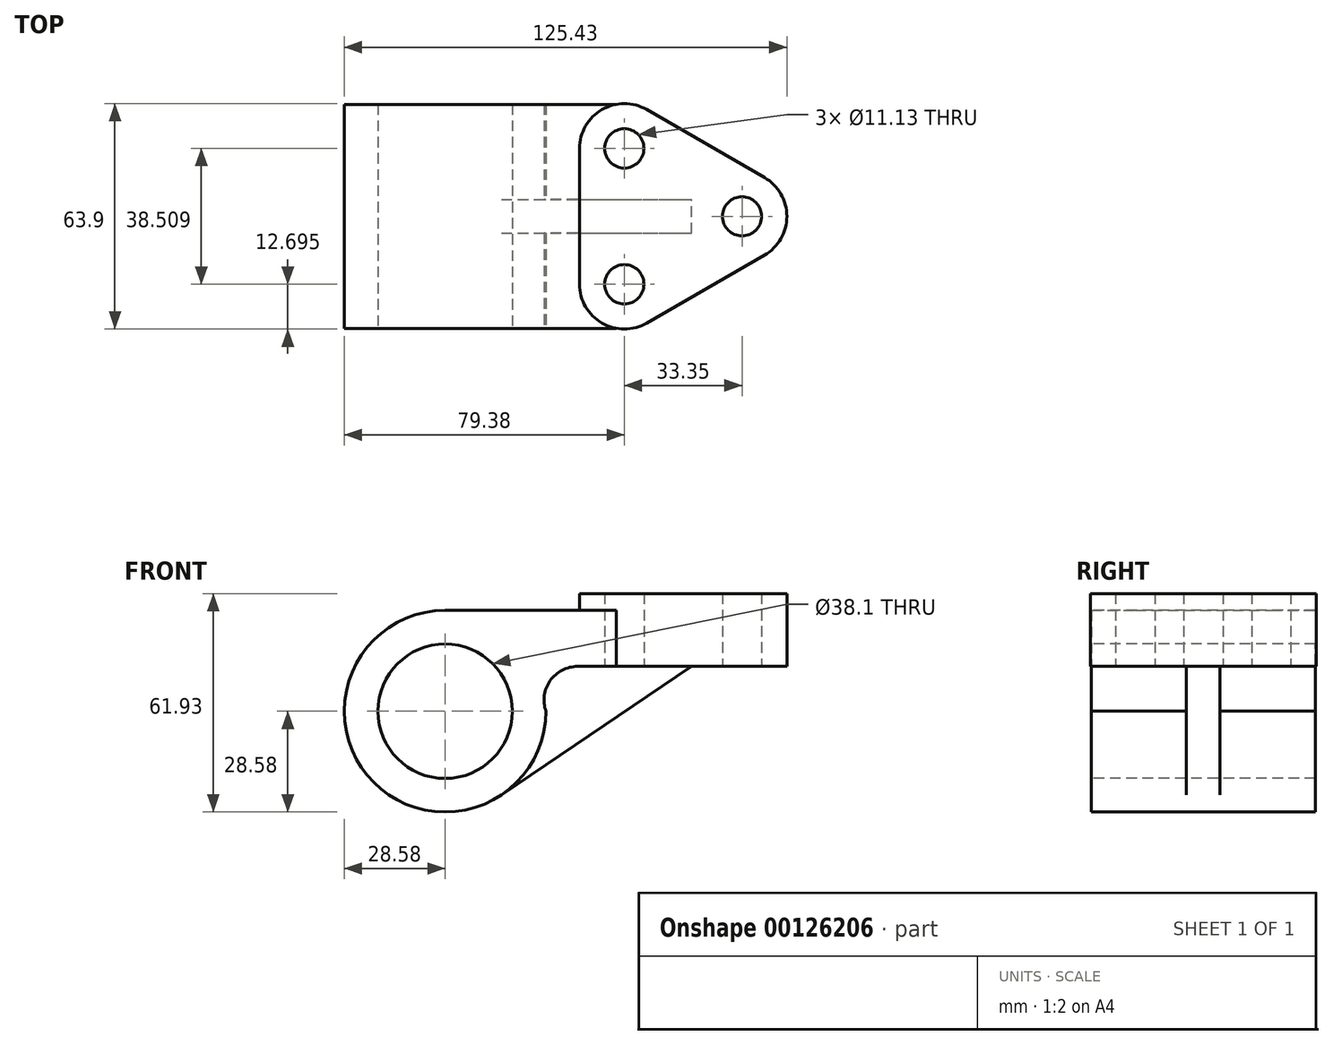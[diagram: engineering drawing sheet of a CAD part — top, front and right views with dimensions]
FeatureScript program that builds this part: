
annotation { "Feature Type Name" : "Feature", "Feature Type Description" : "" }
export const myFeature = defineFeature(function(context is Context, id is Id, definition is map)
    precondition{}
    {
        {
            var Q0;
            Q0=qCreatedBy(makeId("Front.planeOp"),FACE);
            var sketch = newSketch(context, id + "F0", { "sketchPlane" : qUnion([Q0])});
            skCircle(sketch, "E0", {"center": v(0, 0) * mm, "radius": 19.05 * mm});
            skArc(sketch, "E1", {"start": v(37.56, 12.7) * mm, "mid": v(29.78, 8.67) * mm, "end": v(28.58, 0) * mm});
            skLineSegment(sketch, "E2", {"start": v(37.56, 12.7) * mm, "end": v(50.8, 12.7) * mm});
            skLineSegment(sketch, "E3", {"start": v(0, 28.58) * mm, "end": v(50.8, 28.58) * mm});
            skArc(sketch, "E4", {"start": v(0, 28.58) * mm, "mid": v(-20.2, -20.2) * mm, "end": v(28.58, 0) * mm});
            skLineSegment(sketch, "E5", {"start": v(50.8, 28.58) * mm, "end": v(50.8, 12.7) * mm});
            skSolve(sketch);
        }
        {
            var Q0;
            Q0 = qSketchRegion(id + "F0", true);
            extrude(context, id + "F1", {"entities" : qUnion([Q0]), "endBound" : BoundingType.SYMMETRIC, "oppositeDirection" : true, "depth" : 63.5 * mm});
        }
        {
            var Q0;
            Q0=makeQuery(id+"F1.opExtrude","SWEPT_FACE",FACE,{"disambiguationData":[OSD([sQuery(id+"F0.wireOp",EDGE,"E3")])]});
            var sketch = newSketch(context, id + "F2", { "sketchPlane" : qUnion([Q0])});
            skSolve(sketch);
        }
        {
            var Q0;
            {var subQ0=sQuery(id+"F0.wireOp",EDGE,"E3");Q0=makeQuery(id+"F2.imprint","IMPRINT",FACE,{"disambiguationData":[TD([[makeQuery(id+"F2.imprint","IMPRINT",EDGE,{"derivedFrom":makeQuery(id+"F1.opExtrude","CAP_EDGE",EDGE,{"disambiguationData":[OSD([subQ0])],"isStart":true})}),1.0]])]});}
            var sketch = newSketch(context, id + "F3", { "sketchPlane" : qUnion([Q0])});
            skLineSegment(sketch, "E6", {"start": v(0, 0) * mm, "end": v(130.51, 0) * mm, "construction": true});
            skSolve(sketch);
        }
        {
            var Q0;
            Q0=makeQuery(id+"F1.opExtrude","SWEPT_FACE",FACE,{"disambiguationData":[OSD([sQuery(id+"F0.wireOp",EDGE,"E2")])]});
            var sketch = newSketch(context, id + "F4", { "sketchPlane" : qUnion([Q0])});
            skLineSegment(sketch, "E7", {"start": v(90.5, 11) * mm, "end": v(57.15, 30.25) * mm});
            skLineSegment(sketch, "E8", {"start": v(38.1, 19.25) * mm, "end": v(38.1, -19.25) * mm});
            skLineSegment(sketch, "E9", {"start": v(57.15, -30.25) * mm, "end": v(90.5, -11) * mm});
            skPoint(sketch, "E10.visualSharp", {"position": v(109.55, 0) * mm});
            skArc(sketch, "E10.filletArc", {"start": v(90.5, -11) * mm, "mid": v(96.85, 0) * mm, "end": v(90.5, 11) * mm});
            skPoint(sketch, "E11.visualSharp", {"position": v(38.1, 41.25) * mm});
            skArc(sketch, "E11.filletArc", {"start": v(57.15, 30.25) * mm, "mid": v(44.45, 30.25) * mm, "end": v(38.1, 19.25) * mm});
            skPoint(sketch, "E12.visualSharp", {"position": v(38.1, -41.25) * mm});
            skArc(sketch, "E12.filletArc", {"start": v(38.1, -19.25) * mm, "mid": v(44.45, -30.25) * mm, "end": v(57.15, -30.25) * mm});
            skCircle(sketch, "E13", {"center": v(50.8, 19.25) * mm, "radius": 5.56 * mm});
            skCircle(sketch, "E14", {"center": v(50.8, -19.25) * mm, "radius": 5.56 * mm});
            skCircle(sketch, "E15", {"center": v(84.15, 0) * mm, "radius": 5.56 * mm});
            skSolve(sketch);
        }
        {
            var Q0;
            Q0 = qSketchRegion(id + "F4", true);
            extrude(context, id + "F5", {"entities" : qUnion([Q0]), "operationType" : NewBodyOperationType.ADD, "oppositeDirection" : true, "depth" : 20.65 * mm});
        }
        {
            var Q0;
            {var subQ0=sQuery(id+"F4.wireOp",EDGE,"E13");var subQ1=makeQuery(id+"F1.opExtrude","SWEPT_EDGE",EDGE,{"disambiguationData":[OSD([sQuery(id+"F0.wireOp",EDGE,"E2"),sQuery(id+"F0.wireOp",EDGE,"E5")])]});var subQ2=makeQuery(id+"F4.imprint","INTERSECT",VERTEX,{"disambiguationData":[OD(0.0)],"derivedFrom":[subQ1,subQ0]});Q0=makeQuery(id+"F4.imprint","IMPRINT",FACE,{"disambiguationData":[TD([[makeQuery(id+"F4.imprint","IMPRINT",EDGE,{"disambiguationData":[TD([[subQ2,-1.0]])],"derivedFrom":subQ0}),1.0]])]});}
            var Q1;
            {var subQ0=sQuery(id+"F4.wireOp",EDGE,"E14");var subQ1=makeQuery(id+"F1.opExtrude","SWEPT_EDGE",EDGE,{"disambiguationData":[OSD([sQuery(id+"F0.wireOp",EDGE,"E2"),sQuery(id+"F0.wireOp",EDGE,"E5")])]});var subQ2=makeQuery(id+"F4.imprint","INTERSECT",VERTEX,{"disambiguationData":[OD(0.0)],"derivedFrom":[subQ1,subQ0]});Q1=makeQuery(id+"F4.imprint","IMPRINT",FACE,{"disambiguationData":[TD([[makeQuery(id+"F4.imprint","IMPRINT",EDGE,{"disambiguationData":[TD([[subQ2,1.0]])],"derivedFrom":subQ0}),1.0]])]});}
            extrude(context, id + "F6", {"entities" : qUnion([Q0, Q1]), "operationType" : NewBodyOperationType.REMOVE, "endBound" : BoundingType.THROUGH_ALL, "oppositeDirection" : true, "depth" : 25.4 * mm});
        }
        {
            var Q0;
            Q0=qCreatedBy(makeId("Front.planeOp"),FACE);
            var sketch = newSketch(context, id + "F7", { "sketchPlane" : qUnion([Q0])});
            skArc(sketch, "E16.0", {"start": v(37.56, 12.7) * mm, "mid": v(29.78, 8.67) * mm, "end": v(28.58, 0) * mm});
            skLineSegment(sketch, "E17.0", {"start": v(37.56, 12.7) * mm, "end": v(48.53, 12.7) * mm});
            skLineSegment(sketch, "E18.0", {"start": v(57.15, 12.7) * mm, "end": v(48.53, 12.7) * mm});
            skLineSegment(sketch, "E19.0", {"start": v(69.85, 12.7) * mm, "end": v(57.15, 12.7) * mm});
            skArc(sketch, "E20", {"start": v(16, -23.68) * mm, "mid": v(25.23, -13.4) * mm, "end": v(28.57, 0) * mm});
            skLineSegment(sketch, "E21", {"start": v(16, -23.68) * mm, "end": v(69.85, 12.7) * mm});
            skSolve(sketch);
        }
        {
            var Q0;
            Q0 = qSketchRegion(id + "F7", true);
            extrude(context, id + "F8", {"entities" : qUnion([Q0]), "operationType" : NewBodyOperationType.ADD, "endBound" : BoundingType.SYMMETRIC, "depth" : 9.52 * mm});
        }
    });
